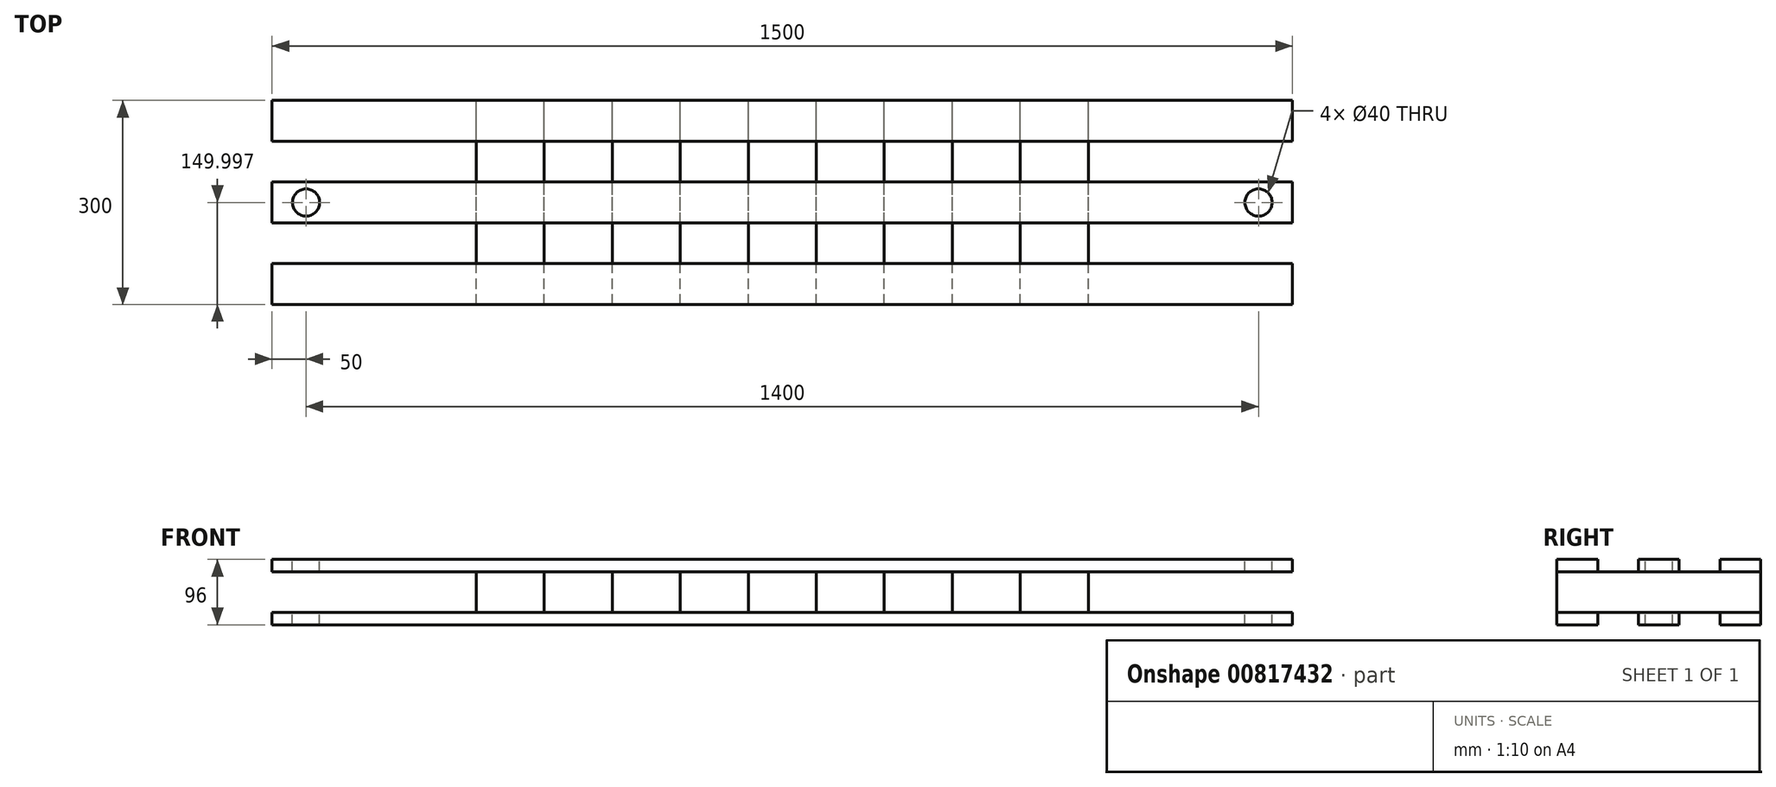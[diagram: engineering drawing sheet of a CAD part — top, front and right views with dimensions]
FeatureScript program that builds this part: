
annotation { "Feature Type Name" : "Feature", "Feature Type Description" : "" }
export const myFeature = defineFeature(function(context is Context, id is Id, definition is map)
    precondition{}
    {
        {
            var Q0;
            Q0=qCreatedBy(makeId("Right.planeOp"),FACE);
            var sketch = newSketch(context, id + "F0", { "sketchPlane" : qUnion([Q0])});
            skLineSegment(sketch, "E0.bottom", {"start": v(-69.57, 93.73) * mm, "end": v(-9.57, 93.73) * mm});
            skLineSegment(sketch, "E0.top", {"start": v(-69.57, 75.73) * mm, "end": v(-9.57, 75.73) * mm});
            skLineSegment(sketch, "E0.left", {"start": v(-69.57, 93.73) * mm, "end": v(-69.57, 75.73) * mm});
            skLineSegment(sketch, "E0.right", {"start": v(-9.57, 93.73) * mm, "end": v(-9.57, 75.73) * mm});
            skLineSegment(sketch, "E1.bottom", {"start": v(50.43, 93.73) * mm, "end": v(110.43, 93.73) * mm});
            skLineSegment(sketch, "E1.top", {"start": v(50.43, 75.73) * mm, "end": v(110.43, 75.73) * mm});
            skLineSegment(sketch, "E1.left", {"start": v(50.43, 93.73) * mm, "end": v(50.43, 75.73) * mm});
            skLineSegment(sketch, "E1.right", {"start": v(110.43, 93.73) * mm, "end": v(110.43, 75.73) * mm});
            skLineSegment(sketch, "E2.bottom", {"start": v(170.43, 93.73) * mm, "end": v(230.43, 93.73) * mm});
            skLineSegment(sketch, "E2.top", {"start": v(170.43, 75.73) * mm, "end": v(230.43, 75.73) * mm});
            skLineSegment(sketch, "E2.left", {"start": v(170.43, 93.73) * mm, "end": v(170.43, 75.73) * mm});
            skLineSegment(sketch, "E2.right", {"start": v(230.43, 93.73) * mm, "end": v(230.43, 75.73) * mm});
            skLineSegment(sketch, "E3.bottom", {"start": v(-69.57, 15.73) * mm, "end": v(-9.57, 15.73) * mm});
            skLineSegment(sketch, "E3.top", {"start": v(-69.57, -2.27) * mm, "end": v(-9.57, -2.27) * mm});
            skLineSegment(sketch, "E3.left", {"start": v(-69.57, 15.73) * mm, "end": v(-69.57, -2.27) * mm});
            skLineSegment(sketch, "E3.right", {"start": v(-9.57, 15.73) * mm, "end": v(-9.57, -2.27) * mm});
            skLineSegment(sketch, "E4.bottom", {"start": v(50.43, 15.73) * mm, "end": v(110.43, 15.73) * mm});
            skLineSegment(sketch, "E4.top", {"start": v(50.43, -2.27) * mm, "end": v(110.43, -2.27) * mm});
            skLineSegment(sketch, "E4.left", {"start": v(50.43, 15.73) * mm, "end": v(50.43, -2.27) * mm});
            skLineSegment(sketch, "E4.right", {"start": v(110.43, 15.73) * mm, "end": v(110.43, -2.27) * mm});
            skLineSegment(sketch, "E5.bottom", {"start": v(170.43, 15.73) * mm, "end": v(230.43, 15.73) * mm});
            skLineSegment(sketch, "E5.top", {"start": v(170.43, -2.27) * mm, "end": v(230.43, -2.27) * mm});
            skLineSegment(sketch, "E5.left", {"start": v(170.43, 15.73) * mm, "end": v(170.43, -2.27) * mm});
            skLineSegment(sketch, "E5.right", {"start": v(230.43, 15.73) * mm, "end": v(230.43, -2.27) * mm});
            skSolve(sketch);
        }
        {
            var Q0;
            Q0 = qSketchRegion(id + "F0", true);
            extrude(context, id + "F1", {"entities" : qUnion([Q0]), "depth" : 1500 * mm, "offsetDistance" : 25 * mm});
        }
        {
            var Q0;
            Q0=makeQuery(id+"F1.opExtrude","SWEPT_FACE",FACE,{"disambiguationData":[OSD([sQuery(id+"F0.wireOp",EDGE,"E2.right")])]});
            var sketch = newSketch(context, id + "F2", { "sketchPlane" : qUnion([Q0])});
            skLineSegment(sketch, "E6.bottom", {"start": v(-300, 75.73) * mm, "end": v(-400, 75.73) * mm});
            skLineSegment(sketch, "E6.top", {"start": v(-300, 15.73) * mm, "end": v(-400, 15.73) * mm});
            skLineSegment(sketch, "E6.left", {"start": v(-300, 75.73) * mm, "end": v(-300, 15.73) * mm});
            skLineSegment(sketch, "E6.right", {"start": v(-400, 75.73) * mm, "end": v(-400, 15.73) * mm});
            skLineSegment(sketch, "E7.bottom", {"start": v(-500, 75.73) * mm, "end": v(-600, 75.73) * mm});
            skLineSegment(sketch, "E7.top", {"start": v(-500, 15.73) * mm, "end": v(-600, 15.73) * mm});
            skLineSegment(sketch, "E7.left", {"start": v(-500, 75.73) * mm, "end": v(-500, 15.73) * mm});
            skLineSegment(sketch, "E7.right", {"start": v(-600, 75.73) * mm, "end": v(-600, 15.73) * mm});
            skLineSegment(sketch, "E8.bottom", {"start": v(-700, 75.73) * mm, "end": v(-800, 75.73) * mm});
            skLineSegment(sketch, "E8.top", {"start": v(-700, 15.73) * mm, "end": v(-800, 15.73) * mm});
            skLineSegment(sketch, "E8.left", {"start": v(-700, 75.73) * mm, "end": v(-700, 15.73) * mm});
            skLineSegment(sketch, "E8.right", {"start": v(-800, 75.73) * mm, "end": v(-800, 15.73) * mm});
            skLineSegment(sketch, "E9.bottom", {"start": v(-900, 75.73) * mm, "end": v(-1000, 75.73) * mm});
            skLineSegment(sketch, "E9.top", {"start": v(-900, 15.73) * mm, "end": v(-1000, 15.73) * mm});
            skLineSegment(sketch, "E9.left", {"start": v(-900, 75.73) * mm, "end": v(-900, 15.73) * mm});
            skLineSegment(sketch, "E9.right", {"start": v(-1000, 75.73) * mm, "end": v(-1000, 15.73) * mm});
            skLineSegment(sketch, "E10.bottom", {"start": v(-1100, 75.73) * mm, "end": v(-1200, 75.73) * mm});
            skLineSegment(sketch, "E10.top", {"start": v(-1100, 15.73) * mm, "end": v(-1200, 15.73) * mm});
            skLineSegment(sketch, "E10.left", {"start": v(-1100, 75.73) * mm, "end": v(-1100, 15.73) * mm});
            skLineSegment(sketch, "E10.right", {"start": v(-1200, 75.73) * mm, "end": v(-1200, 15.73) * mm});
            skSolve(sketch);
        }
        {
            var Q0;
            Q0 = qSketchRegion(id + "F2", true);
            extrude(context, id + "F3", {"entities" : qUnion([Q0]), "oppositeDirection" : true, "depth" : 300 * mm, "offsetDistance" : 25 * mm});
        }
        {
            var Q0;
            Q0=makeQuery(id+"F1.opExtrude","SWEPT_FACE",FACE,{"disambiguationData":[OSD([sQuery(id+"F0.wireOp",EDGE,"E1.bottom")])]});
            var sketch = newSketch(context, id + "F4", { "sketchPlane" : qUnion([Q0])});
            skCircle(sketch, "E11", {"center": v(50, 80.43) * mm, "radius": 20 * mm});
            skCircle(sketch, "E12", {"center": v(1450, 80.43) * mm, "radius": 20 * mm});
            skPoint(sketch, "E13", {"position": v(1500, 80.43) * mm});
            skSolve(sketch);
        }
        {
            var Q0;
            Q0 = qSketchRegion(id + "F4", true);
            var Q1;
            Q1=makeQuery(id+"F1.opExtrude","SWEPT_FACE",FACE,{"disambiguationData":[OSD([sQuery(id+"F0.wireOp",EDGE,"E4.top")])]});
            extrude(context, id + "F5", {"entities" : qUnion([Q0]), "operationType" : NewBodyOperationType.REMOVE, "endBound" : BoundingType.UP_TO_SURFACE, "oppositeDirection" : true, "depth" : 25 * mm, "endBoundEntityFace" : qUnion([Q1]), "offsetDistance" : 25 * mm});
        }
    });
